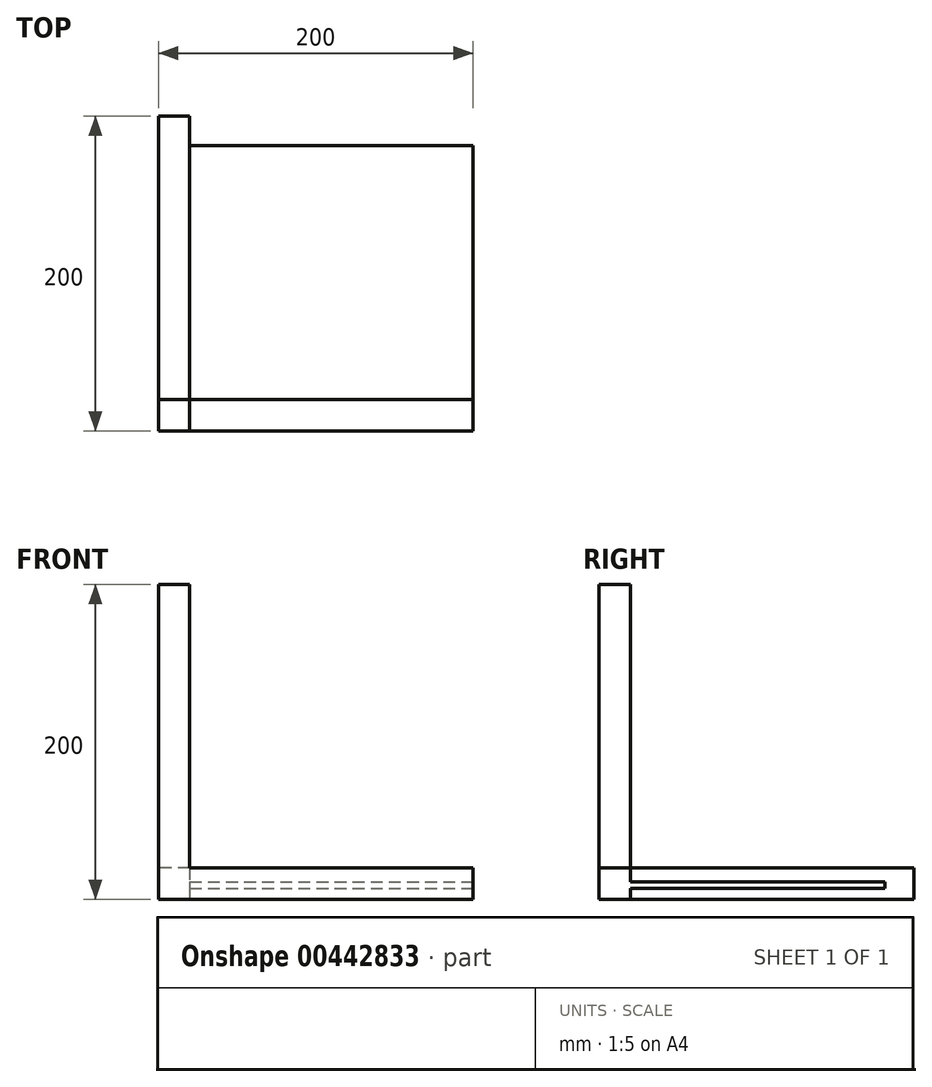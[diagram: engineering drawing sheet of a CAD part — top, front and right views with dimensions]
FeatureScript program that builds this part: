
annotation { "Feature Type Name" : "Feature", "Feature Type Description" : "" }
export const myFeature = defineFeature(function(context is Context, id is Id, definition is map)
    precondition{}
    {
        {
            var Q0;
            Q0=qCreatedBy(makeId("Top.planeOp"),FACE);
            var sketch = newSketch(context, id + "F0", { "sketchPlane" : qUnion([Q0])});
            skLineSegment(sketch, "E0.bottom", {"start": v(0, 0) * mm, "end": v(200, 0) * mm});
            skLineSegment(sketch, "E0.top", {"start": v(0, 20) * mm, "end": v(200, 20) * mm});
            skLineSegment(sketch, "E0.left", {"start": v(0, 0) * mm, "end": v(0, 20) * mm});
            skLineSegment(sketch, "E0.right", {"start": v(200, 0) * mm, "end": v(200, 20) * mm});
            skSolve(sketch);
        }
        {
            var Q0;
            Q0=qSketchRegion(id+"F0",true);
            extrude(context, id + "F1", {"entities" : qUnion([Q0]), "depth" : 20 * mm});
        }
        {
            var Q0;
            Q0=makeQuery(id+"F1.opExtrude","CAP_FACE",FACE,{"disambiguationData":[OSD([sQuery(id+"F0.wireOp",EDGE,"E0.bottom"),sQuery(id+"F0.wireOp",EDGE,"E0.top"),sQuery(id+"F0.wireOp",EDGE,"E0.left"),sQuery(id+"F0.wireOp",EDGE,"E0.right")])],"isStart":false});
            var sketch = newSketch(context, id + "F2", { "sketchPlane" : qUnion([Q0])});
            skLineSegment(sketch, "E1.bottom", {"start": v(0, 0) * mm, "end": v(20, 0) * mm});
            skLineSegment(sketch, "E1.top", {"start": v(0, 20) * mm, "end": v(20, 20) * mm});
            skLineSegment(sketch, "E1.left", {"start": v(0, 0) * mm, "end": v(0, 20) * mm});
            skLineSegment(sketch, "E1.right", {"start": v(20, 0) * mm, "end": v(20, 20) * mm});
            skSolve(sketch);
        }
        {
            var Q0;
            Q0=qSketchRegion(id+"F2",true);
            extrude(context, id + "F3", {"entities" : qUnion([Q0]), "operationType" : NewBodyOperationType.ADD, "depth" : 180 * mm});
        }
        {
            var Q0;
            Q0=makeQuery(id+"F3.boolean.opBoolean","MERGE",FACE,{"derivedFrom":[makeQuery(id+"F1.opExtrude","SWEPT_FACE",FACE,{"disambiguationData":[OSD([sQuery(id+"F0.wireOp",EDGE,"E0.top")])]}),makeQuery(id+"F3.opExtrude","SWEPT_FACE",FACE,{"disambiguationData":[OSD([sQuery(id+"F2.wireOp",EDGE,"E1.top")])]})]});
            var sketch = newSketch(context, id + "F4", { "sketchPlane" : qUnion([Q0])});
            skLineSegment(sketch, "E2.bottom", {"start": v(-20, 20) * mm, "end": v(0, 20) * mm});
            skLineSegment(sketch, "E2.top", {"start": v(-20, 0) * mm, "end": v(0, 0) * mm});
            skLineSegment(sketch, "E2.left", {"start": v(-20, 20) * mm, "end": v(-20, 0) * mm});
            skLineSegment(sketch, "E2.right", {"start": v(0, 20) * mm, "end": v(0, 0) * mm});
            skSolve(sketch);
        }
        {
            var Q0;
            Q0=qSketchRegion(id+"F4",true);
            extrude(context, id + "F5", {"entities" : qUnion([Q0]), "operationType" : NewBodyOperationType.ADD, "depth" : 180 * mm});
        }
        {
            var Q0;
            {var subQ0=sQuery(id+"F0.wireOp",EDGE,"E0.right");var subQ1=sQuery(id+"F0.wireOp",EDGE,"E0.top");var subQ2=makeQuery(id+"F1.opExtrude","SWEPT_FACE",FACE,{"disambiguationData":[OSD([subQ1])]});var subQ5=makeQuery(id+"F3.opExtrude","SWEPT_FACE",FACE,{"disambiguationData":[OSD([sQuery(id+"F2.wireOp",EDGE,"E1.top")])]});Q0=makeQuery(id+"F5.boolean.opBoolean","SPLIT",FACE,{"disambiguationData":[TD([makeQuery(id+"F1.opExtrude","SWEPT_FACE",FACE,{"disambiguationData":[OSD([subQ0])]})])],"derivedFrom":makeQuery(id+"F3.boolean.opBoolean","MERGE",FACE,{"derivedFrom":[subQ2,subQ5]})});}
            var sketch = newSketch(context, id + "F6", { "sketchPlane" : qUnion([Q0])});
            skLineSegment(sketch, "E3.bottom", {"start": v(-20, 11) * mm, "end": v(-200, 11) * mm});
            skLineSegment(sketch, "E3.top", {"start": v(-20, 7) * mm, "end": v(-200, 7) * mm});
            skLineSegment(sketch, "E3.left", {"start": v(-20, 11) * mm, "end": v(-20, 7) * mm});
            skLineSegment(sketch, "E3.right", {"start": v(-200, 11) * mm, "end": v(-200, 7) * mm});
            skSolve(sketch);
        }
        {
            var Q0;
            Q0=makeQuery(id+"F6.imprint","IMPRINT",FACE,{"disambiguationData":[TD([[makeQuery(id+"F6.imprint","IMPRINT",EDGE,{"derivedFrom":sQuery(id+"F6.wireOp",EDGE,"E3.bottom")}),1.0]])]});
            extrude(context, id + "F7", {"entities" : qUnion([Q0]), "operationType" : NewBodyOperationType.ADD, "depth" : 161.4 * mm});
        }
    });
